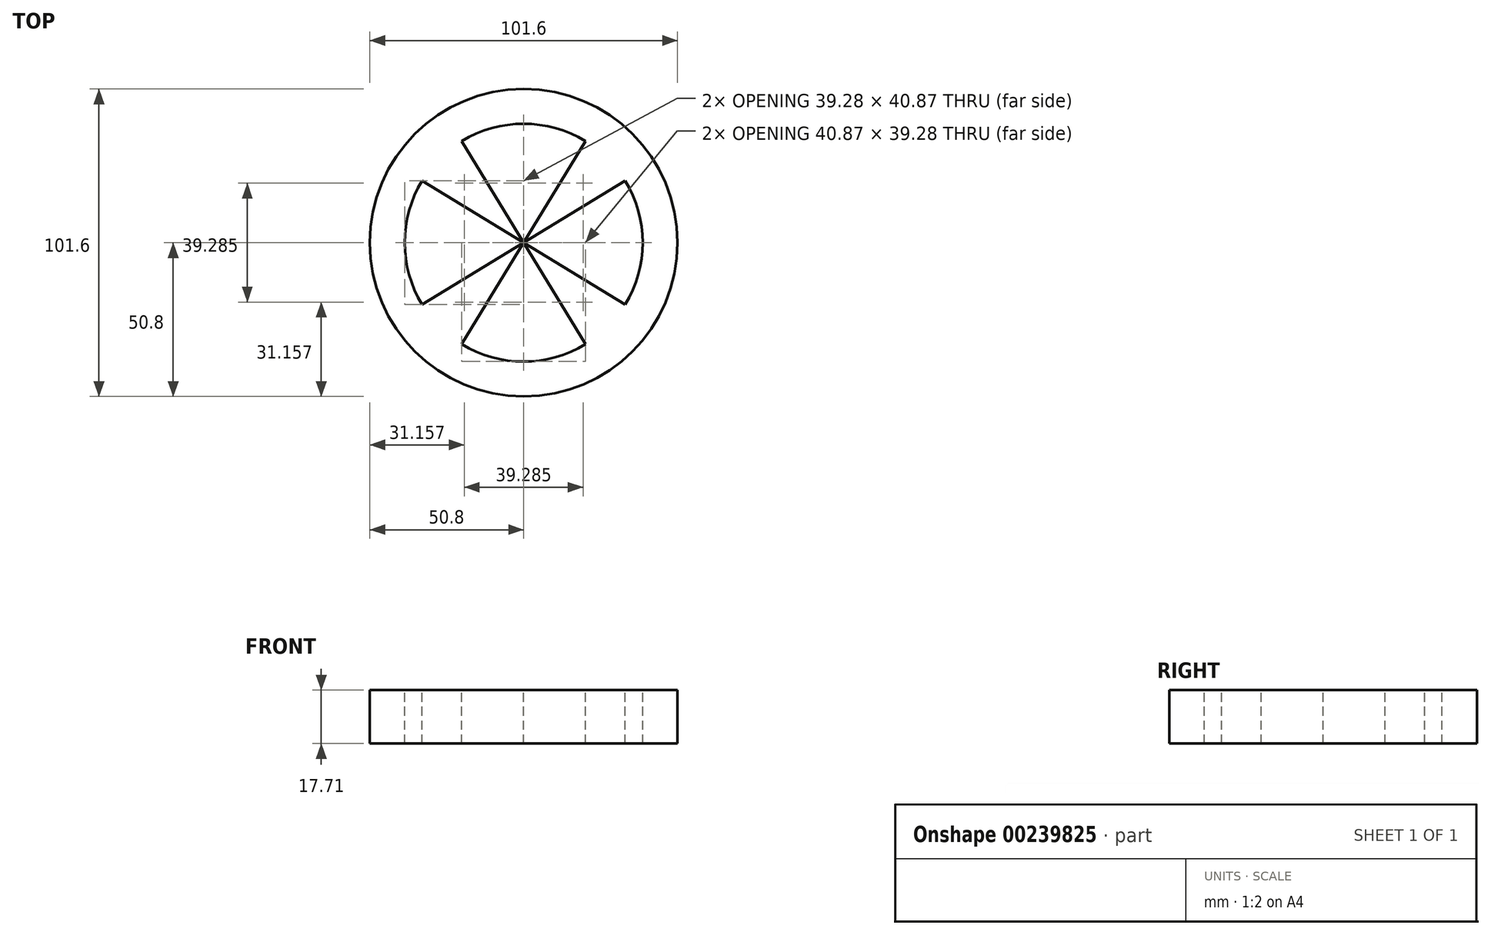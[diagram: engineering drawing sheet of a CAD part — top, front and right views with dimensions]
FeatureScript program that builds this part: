
annotation { "Feature Type Name" : "Feature", "Feature Type Description" : "" }
export const myFeature = defineFeature(function(context is Context, id is Id, definition is map)
    precondition{}
    {
        {
            var Q0;
            Q0=qCreatedBy(makeId("Front.planeOp"),FACE);
            var sketch = newSketch(context, id + "F0", { "sketchPlane" : qUnion([Q0])});
            skLineSegment(sketch, "E0.bottom", {"start": v(0, 0) * mm, "end": v(-50.8, 0) * mm});
            skLineSegment(sketch, "E0.top", {"start": v(0, -17.71) * mm, "end": v(-50.8, -17.71) * mm});
            skLineSegment(sketch, "E0.left", {"start": v(0, 0) * mm, "end": v(0, -17.71) * mm});
            skLineSegment(sketch, "E0.right", {"start": v(-50.8, 0) * mm, "end": v(-50.8, -17.71) * mm});
            skSolve(sketch);
        }
        {
            var Q0;
            Q0 = qSketchRegion(id + "F0", true);
            var Q1;
            Q1=sQuery(id+"F0.wireOp",EDGE,"E0.left");
            revolve(context, id + "F1", {"entities" : qUnion([Q0]), "axis" : qUnion([Q1]), "revolveType" : RevolveType.FULL});
        }
        {
            var Q0;
            Q0=makeQuery(id+"F1.opRevolve","SWEPT_FACE",FACE,{"disambiguationData":[OSD([sQuery(id+"F0.wireOp",EDGE,"E0.bottom")])]});
            var sketch = newSketch(context, id + "F2", { "sketchPlane" : qUnion([Q0])});
            skLineSegment(sketch, "E1", {"start": v(0, 0) * mm, "end": v(-20.44, 33.55) * mm});
            skLineSegment(sketch, "E2", {"start": v(0, 0) * mm, "end": v(20.44, 33.55) * mm});
            skArc(sketch, "E3", {"start": v(20.44, 33.55) * mm, "mid": v(0, 39.28) * mm, "end": v(-20.44, 33.55) * mm});
            skLineSegment(sketch, "E4", {"start": v(0, 0) * mm, "end": v(0, 39.28) * mm, "construction": true});
            skLineSegment(sketch, "E5", {"start": v(-20.44, 33.55) * mm, "end": v(0, 39.28) * mm, "construction": true});
            skLineSegment(sketch, "E6", {"start": v(20.44, 33.55) * mm, "end": v(0, 39.28) * mm, "construction": true});
            skSolve(sketch);
        }
        {
            var Q0;
            Q0 = qSketchRegion(id + "F2", true);
            extrude(context, id + "F3", {"entities" : qUnion([Q0]), "operationType" : NewBodyOperationType.REMOVE, "oppositeDirection" : true, "depth" : 25.4 * mm});
        }
        {
            var Q0;
            Q0=makeQuery(id+"F1.opRevolve","SWEPT_BODY",BODY,{"disambiguationData":[OSD([sQuery(id+"F0.wireOp",EDGE,"E0.bottom"),sQuery(id+"F0.wireOp",EDGE,"E0.top"),sQuery(id+"F0.wireOp",EDGE,"E0.left"),sQuery(id+"F0.wireOp",EDGE,"E0.right")])]});
            var Q1;
            Q1=makeQuery(id+"F1.opRevolve","SWEPT_EDGE",EDGE,{"disambiguationData":[OSD([sQuery(id+"F0.wireOp",EDGE,"E0.bottom"),sQuery(id+"F0.wireOp",EDGE,"E0.right")])]});
            circularPattern(context, id + "F4", {"entities" : qUnion([Q0]), "axis" : qUnion([Q1]), "angle" : 360 * degree, "instanceCount" : 4, "equalSpace" : true});
        }
    });
